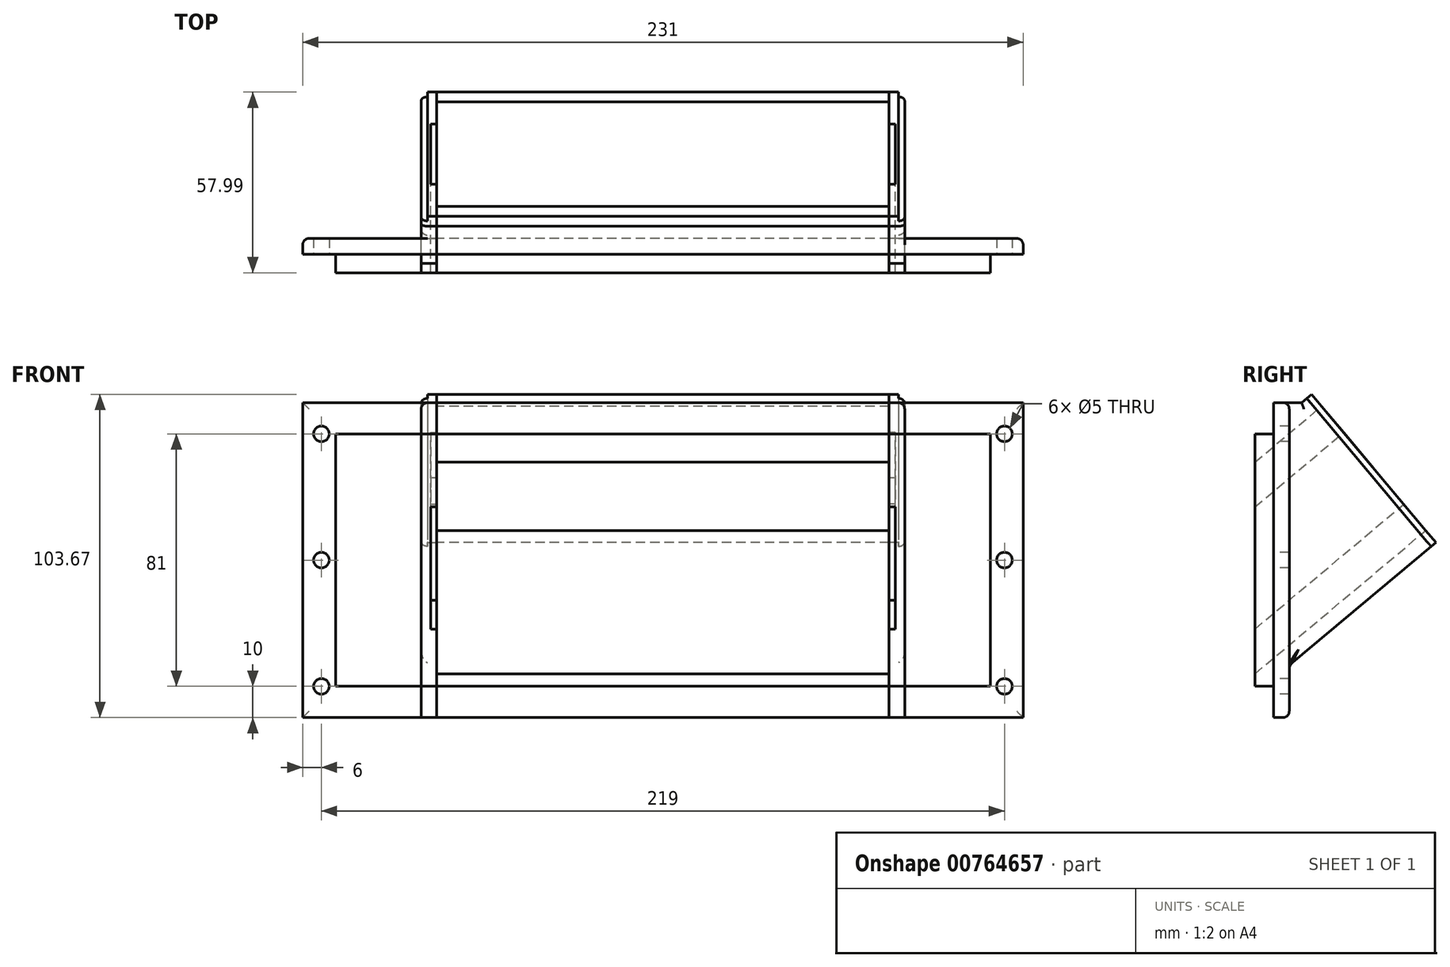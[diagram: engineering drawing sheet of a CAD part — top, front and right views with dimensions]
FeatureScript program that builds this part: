
annotation { "Feature Type Name" : "Feature", "Feature Type Description" : "" }
export const myFeature = defineFeature(function(context is Context, id is Id, definition is map)
    precondition{}
    {
        {
            var Q0;
            Q0=qCreatedBy(makeId("Right.planeOp"),FACE);
            var sketch = newSketch(context, id + "F0", { "sketchPlane" : qUnion([Q0])});
            skLineSegment(sketch, "E0", {"start": v(-6, 71.92) * mm, "end": v(-6, 81) * mm});
            skLineSegment(sketch, "E1", {"start": v(-6, 0) * mm, "end": v(-6, 4.04) * mm});
            skLineSegment(sketch, "E2", {"start": v(-6, 81) * mm, "end": v(0, 81) * mm});
            skLineSegment(sketch, "E3", {"start": v(-6, 0) * mm, "end": v(0, 0) * mm});
            skLineSegment(sketch, "E4", {"start": v(-3, 0.03) * mm, "end": v(-3, 0) * mm});
            skLineSegment(sketch, "E5", {"start": v(-3, 81) * mm, "end": v(-3, 80.97) * mm});
            skLineSegment(sketch, "E6", {"start": v(-6, 71.92) * mm, "end": v(15.35, 89.84) * mm});
            skLineSegment(sketch, "E7", {"start": v(-6, 4.04) * mm, "end": v(48.78, 50) * mm});
            skLineSegment(sketch, "E8", {"start": v(52, 46.18) * mm, "end": v(48.78, 50) * mm});
            skLineSegment(sketch, "E9", {"start": v(15.35, 89.84) * mm, "end": v(12.14, 93.67) * mm});
            skLineSegment(sketch, "E10", {"start": v(8.96, 91) * mm, "end": v(12.14, 93.67) * mm});
            skLineSegment(sketch, "E11", {"start": v(-3, 80.97) * mm, "end": v(-2.96, 81) * mm});
            skLineSegment(sketch, "E12", {"start": v(5, 6.75) * mm, "end": v(52, 46.18) * mm});
            skLineSegment(sketch, "E13", {"start": v(-3.04, 0) * mm, "end": v(-3, 0.03) * mm});
            skLineSegment(sketch, "E14", {"start": v(0, -10) * mm, "end": v(0, 0) * mm});
            skLineSegment(sketch, "E15", {"start": v(0, 81) * mm, "end": v(0, 91) * mm});
            skLineSegment(sketch, "E16", {"start": v(0, -10) * mm, "end": v(5, -10) * mm});
            skLineSegment(sketch, "E17", {"start": v(5, -10) * mm, "end": v(5, -5) * mm});
            skLineSegment(sketch, "E18", {"start": v(5, -5) * mm, "end": v(5, 0) * mm});
            skLineSegment(sketch, "E19", {"start": v(5, 0) * mm, "end": v(5, 5) * mm});
            skLineSegment(sketch, "E20", {"start": v(5, 5) * mm, "end": v(5, 6.75) * mm});
            skLineSegment(sketch, "E21", {"start": v(0, 91) * mm, "end": v(5, 91) * mm});
            skLineSegment(sketch, "E22", {"start": v(5, 91) * mm, "end": v(8.96, 91) * mm});
            skSolve(sketch);
        }
        {
            var Q0;
            Q0 = qSketchRegion(id + "F0", true);
            extrude(context, id + "F1", {"entities" : qUnion([Q0]), "depth" : 145 * mm, "offsetDistance" : 25 * mm});
        }
        {
            var Q0;
            Q0=qCreatedBy(makeId("Right.planeOp"),FACE);
            var sketch = newSketch(context, id + "F2", { "sketchPlane" : qUnion([Q0])});
            skLineSegment(sketch, "E23", {"start": v(-6, 71.92) * mm, "end": v(-6, 81) * mm});
            skLineSegment(sketch, "E24", {"start": v(-6, 0) * mm, "end": v(-6, 4.04) * mm});
            skLineSegment(sketch, "E25", {"start": v(-6, 81) * mm, "end": v(0, 81) * mm});
            skLineSegment(sketch, "E26", {"start": v(-6, 0) * mm, "end": v(0, 0) * mm});
            skLineSegment(sketch, "E27", {"start": v(-3, 0.03) * mm, "end": v(-3, 0) * mm});
            skLineSegment(sketch, "E28", {"start": v(-3, 81) * mm, "end": v(-3, 80.97) * mm});
            skLineSegment(sketch, "E29", {"start": v(52, 46.18) * mm, "end": v(48.78, 50) * mm});
            skLineSegment(sketch, "E30", {"start": v(15.35, 89.84) * mm, "end": v(12.14, 93.67) * mm});
            skLineSegment(sketch, "E31", {"start": v(8.96, 91) * mm, "end": v(12.14, 93.67) * mm});
            skLineSegment(sketch, "E32", {"start": v(-3, 80.97) * mm, "end": v(-2.96, 81) * mm});
            skLineSegment(sketch, "E33", {"start": v(5, 6.75) * mm, "end": v(52, 46.18) * mm});
            skLineSegment(sketch, "E34", {"start": v(-3.04, 0) * mm, "end": v(-3, 0.03) * mm});
            skLineSegment(sketch, "E35", {"start": v(0, -10) * mm, "end": v(0, 0) * mm});
            skLineSegment(sketch, "E36", {"start": v(0, 81) * mm, "end": v(0, 91) * mm});
            skLineSegment(sketch, "E37", {"start": v(0, -10) * mm, "end": v(5, -10) * mm});
            skLineSegment(sketch, "E38", {"start": v(5, -10) * mm, "end": v(5, -5) * mm});
            skLineSegment(sketch, "E39", {"start": v(5, -5) * mm, "end": v(5, 0) * mm});
            skLineSegment(sketch, "E40", {"start": v(5, 0) * mm, "end": v(5, 5) * mm});
            skLineSegment(sketch, "E41", {"start": v(5, 5) * mm, "end": v(5, 6.75) * mm});
            skLineSegment(sketch, "E42", {"start": v(0, 91) * mm, "end": v(5, 91) * mm});
            skLineSegment(sketch, "E43", {"start": v(5, 91) * mm, "end": v(8.96, 91) * mm});
            skLineSegment(sketch, "E44", {"start": v(15.35, 89.84) * mm, "end": v(48.78, 50) * mm});
            skLineSegment(sketch, "E45", {"start": v(-6, 71.92) * mm, "end": v(-6, 4.04) * mm});
            skSolve(sketch);
        }
        {
            var Q0;
            {var subQ5=sQuery(id+"F2.wireOp",EDGE,"E23");Q0=makeQuery(id+"F2.imprint","IMPRINT",FACE,{"disambiguationData":[TD([[makeQuery(id+"F2.imprint","IMPRINT",EDGE,{"derivedFrom":subQ5}),-1.0]])]});}
            extrude(context, id + "F3", {"entities" : qUnion([Q0]), "depth" : -5 * mm, "offsetDistance" : 25 * mm});
        }
        {
            var Q0;
            Q0=qCreatedBy(makeId("Right.planeOp"),FACE);
            var sketch = newSketch(context, id + "F4", { "sketchPlane" : qUnion([Q0])});
            skLineSegment(sketch, "E46", {"start": v(-6, 71.92) * mm, "end": v(-6, 81) * mm});
            skLineSegment(sketch, "E47", {"start": v(-6, 0) * mm, "end": v(-6, 4.04) * mm});
            skLineSegment(sketch, "E48", {"start": v(-6, 81) * mm, "end": v(0, 81) * mm});
            skLineSegment(sketch, "E49", {"start": v(-6, 0) * mm, "end": v(0, 0) * mm});
            skLineSegment(sketch, "E50", {"start": v(-3, 0.03) * mm, "end": v(-3, 0) * mm});
            skLineSegment(sketch, "E51", {"start": v(-3, 81) * mm, "end": v(-3, 80.97) * mm});
            skLineSegment(sketch, "E52", {"start": v(52, 46.18) * mm, "end": v(48.78, 50) * mm});
            skLineSegment(sketch, "E53", {"start": v(15.35, 89.84) * mm, "end": v(12.14, 93.67) * mm});
            skLineSegment(sketch, "E54", {"start": v(8.96, 91) * mm, "end": v(12.14, 93.67) * mm});
            skLineSegment(sketch, "E55", {"start": v(-3, 80.97) * mm, "end": v(-2.96, 81) * mm});
            skLineSegment(sketch, "E56", {"start": v(5, 6.75) * mm, "end": v(52, 46.18) * mm});
            skLineSegment(sketch, "E57", {"start": v(-3.04, 0) * mm, "end": v(-3, 0.03) * mm});
            skLineSegment(sketch, "E58", {"start": v(0, -10) * mm, "end": v(0, 0) * mm});
            skLineSegment(sketch, "E59", {"start": v(0, 81) * mm, "end": v(0, 91) * mm});
            skLineSegment(sketch, "E60", {"start": v(0, -10) * mm, "end": v(5, -10) * mm});
            skLineSegment(sketch, "E61", {"start": v(5, -10) * mm, "end": v(5, -5) * mm});
            skLineSegment(sketch, "E62", {"start": v(5, -5) * mm, "end": v(5, 0) * mm});
            skLineSegment(sketch, "E63", {"start": v(5, 0) * mm, "end": v(5, 5) * mm});
            skLineSegment(sketch, "E64", {"start": v(5, 5) * mm, "end": v(5, 6.75) * mm});
            skLineSegment(sketch, "E65", {"start": v(0, 91) * mm, "end": v(5, 91) * mm});
            skLineSegment(sketch, "E66", {"start": v(5, 91) * mm, "end": v(8.96, 91) * mm});
            skLineSegment(sketch, "E67", {"start": v(15.35, 89.84) * mm, "end": v(48.78, 50) * mm});
            skLineSegment(sketch, "E68", {"start": v(-6, 71.92) * mm, "end": v(-6, 4.04) * mm});
            skSolve(sketch);
        }
        {
            var Q0;
            Q0=qCreatedBy(makeId("Right.planeOp"),FACE);
            cPlane(context, id + "F5", {"entities" : qUnion([Q0]), "cplaneType" : CPlaneType.OFFSET, "offset" : 145 * mm, "width" : 150 * mm, "height" : 150 * mm});
        }
        {
            var Q0;
            Q0=qCreatedBy(id+"F5.planeOp",FACE);
            var sketch = newSketch(context, id + "F6", { "sketchPlane" : qUnion([Q0])});
            skLineSegment(sketch, "E69", {"start": v(-6, 71.92) * mm, "end": v(-6, 81) * mm});
            skLineSegment(sketch, "E70", {"start": v(-6, 0) * mm, "end": v(-6, 4.04) * mm});
            skLineSegment(sketch, "E71", {"start": v(-6, 81) * mm, "end": v(0, 81) * mm});
            skLineSegment(sketch, "E72", {"start": v(-6, 0) * mm, "end": v(0, 0) * mm});
            skLineSegment(sketch, "E73", {"start": v(-3, 0.03) * mm, "end": v(-3, 0) * mm});
            skLineSegment(sketch, "E74", {"start": v(-3, 81) * mm, "end": v(-3, 80.97) * mm});
            skLineSegment(sketch, "E75", {"start": v(52, 46.18) * mm, "end": v(48.78, 50) * mm});
            skLineSegment(sketch, "E76", {"start": v(15.35, 89.84) * mm, "end": v(12.14, 93.67) * mm});
            skLineSegment(sketch, "E77", {"start": v(8.96, 91) * mm, "end": v(12.14, 93.67) * mm});
            skLineSegment(sketch, "E78", {"start": v(-3, 80.97) * mm, "end": v(-2.96, 81) * mm});
            skLineSegment(sketch, "E79", {"start": v(5, 6.75) * mm, "end": v(52, 46.18) * mm});
            skLineSegment(sketch, "E80", {"start": v(-3.04, 0) * mm, "end": v(-3, 0.03) * mm});
            skLineSegment(sketch, "E81", {"start": v(0, -10) * mm, "end": v(0, 0) * mm});
            skLineSegment(sketch, "E82", {"start": v(0, 81) * mm, "end": v(0, 91) * mm});
            skLineSegment(sketch, "E83", {"start": v(0, -10) * mm, "end": v(5, -10) * mm});
            skLineSegment(sketch, "E84", {"start": v(5, -10) * mm, "end": v(5, -5) * mm});
            skLineSegment(sketch, "E85", {"start": v(5, -5) * mm, "end": v(5, 0) * mm});
            skLineSegment(sketch, "E86", {"start": v(5, 0) * mm, "end": v(5, 5) * mm});
            skLineSegment(sketch, "E87", {"start": v(5, 5) * mm, "end": v(5, 6.75) * mm});
            skLineSegment(sketch, "E88", {"start": v(0, 91) * mm, "end": v(5, 91) * mm});
            skLineSegment(sketch, "E89", {"start": v(5, 91) * mm, "end": v(8.96, 91) * mm});
            skLineSegment(sketch, "E90", {"start": v(15.35, 89.84) * mm, "end": v(48.78, 50) * mm});
            skLineSegment(sketch, "E91", {"start": v(-6, 71.92) * mm, "end": v(-6, 4.04) * mm});
            skSolve(sketch);
        }
        {
            var Q0;
            {var subQ5=sQuery(id+"F6.wireOp",EDGE,"E69");Q0=makeQuery(id+"F6.imprint","IMPRINT",FACE,{"disambiguationData":[TD([[makeQuery(id+"F6.imprint","IMPRINT",EDGE,{"derivedFrom":subQ5}),-1.0]])]});}
            extrude(context, id + "F7", {"entities" : qUnion([Q0]), "depth" : 5 * mm, "offsetDistance" : 25 * mm});
        }
        {
            var Q0;
            Q0=qCreatedBy(id+"F5.planeOp",FACE);
            var sketch = newSketch(context, id + "F8", { "sketchPlane" : qUnion([Q0])});
            skLineSegment(sketch, "E92", {"start": v(-6, 71.92) * mm, "end": v(-6, 81) * mm});
            skLineSegment(sketch, "E93", {"start": v(-6, 0) * mm, "end": v(-6, 4.04) * mm});
            skLineSegment(sketch, "E94", {"start": v(-6, 81) * mm, "end": v(0, 81) * mm});
            skLineSegment(sketch, "E95", {"start": v(-6, 0) * mm, "end": v(0, 0) * mm});
            skLineSegment(sketch, "E96", {"start": v(-3, 0.03) * mm, "end": v(-3, 0) * mm});
            skLineSegment(sketch, "E97", {"start": v(-3, 81) * mm, "end": v(-3, 80.97) * mm});
            skLineSegment(sketch, "E98", {"start": v(-3, 80.97) * mm, "end": v(-2.96, 81) * mm});
            skLineSegment(sketch, "E99", {"start": v(-3.04, 0) * mm, "end": v(-3, 0.03) * mm});
            skLineSegment(sketch, "E100", {"start": v(0, -10) * mm, "end": v(0, 0) * mm});
            skLineSegment(sketch, "E101", {"start": v(0, 81) * mm, "end": v(0, 91) * mm});
            skLineSegment(sketch, "E102", {"start": v(0, -10) * mm, "end": v(5, -10) * mm});
            skLineSegment(sketch, "E103", {"start": v(5, -10) * mm, "end": v(5, -5) * mm});
            skLineSegment(sketch, "E104", {"start": v(5, -5) * mm, "end": v(5, 0) * mm});
            skLineSegment(sketch, "E105", {"start": v(5, 0) * mm, "end": v(5, 5) * mm});
            skLineSegment(sketch, "E106", {"start": v(5, 5) * mm, "end": v(5, 6.75) * mm});
            skLineSegment(sketch, "E107", {"start": v(0, 91) * mm, "end": v(5, 91) * mm});
            skLineSegment(sketch, "E108", {"start": v(-6, 71.92) * mm, "end": v(-6, 4.04) * mm});
            skLineSegment(sketch, "E109", {"start": v(5, 6.75) * mm, "end": v(5, 91) * mm});
            skSolve(sketch);
        }
        {
            var Q0;
            Q0 = qSketchRegion(id + "F8", true);
            extrude(context, id + "F9", {"entities" : qUnion([Q0]), "depth" : 43 * mm, "offsetDistance" : 25 * mm});
        }
        {
            var Q0;
            Q0=qCreatedBy(makeId("Right.planeOp"),FACE);
            var sketch = newSketch(context, id + "F10", { "sketchPlane" : qUnion([Q0])});
            skLineSegment(sketch, "E110", {"start": v(-6, 71.92) * mm, "end": v(-6, 81) * mm});
            skLineSegment(sketch, "E111", {"start": v(-6, 0) * mm, "end": v(-6, 4.04) * mm});
            skLineSegment(sketch, "E112", {"start": v(-6, 81) * mm, "end": v(0, 81) * mm});
            skLineSegment(sketch, "E113", {"start": v(-6, 0) * mm, "end": v(0, 0) * mm});
            skLineSegment(sketch, "E114", {"start": v(-3, 0.03) * mm, "end": v(-3, 0) * mm});
            skLineSegment(sketch, "E115", {"start": v(-3, 81) * mm, "end": v(-3, 80.97) * mm});
            skLineSegment(sketch, "E116", {"start": v(-3, 80.97) * mm, "end": v(-2.96, 81) * mm});
            skLineSegment(sketch, "E117", {"start": v(-3.04, 0) * mm, "end": v(-3, 0.03) * mm});
            skLineSegment(sketch, "E118", {"start": v(0, -10) * mm, "end": v(0, 0) * mm});
            skLineSegment(sketch, "E119", {"start": v(0, 81) * mm, "end": v(0, 91) * mm});
            skLineSegment(sketch, "E120", {"start": v(0, -10) * mm, "end": v(5, -10) * mm});
            skLineSegment(sketch, "E121", {"start": v(5, -10) * mm, "end": v(5, -5) * mm});
            skLineSegment(sketch, "E122", {"start": v(5, -5) * mm, "end": v(5, 0) * mm});
            skLineSegment(sketch, "E123", {"start": v(5, 0) * mm, "end": v(5, 5) * mm});
            skLineSegment(sketch, "E124", {"start": v(5, 5) * mm, "end": v(5, 6.75) * mm});
            skLineSegment(sketch, "E125", {"start": v(0, 91) * mm, "end": v(5, 91) * mm});
            skLineSegment(sketch, "E126", {"start": v(-6, 71.92) * mm, "end": v(-6, 4.04) * mm});
            skLineSegment(sketch, "E127", {"start": v(5, 6.75) * mm, "end": v(5, 91) * mm});
            skSolve(sketch);
        }
        {
            var Q0;
            Q0 = qSketchRegion(id + "F10", true);
            extrude(context, id + "F11", {"entities" : qUnion([Q0]), "depth" : -43 * mm, "offsetDistance" : 25 * mm});
        }
        {
            var Q0;
            Q0=qCreatedBy(makeId("Front.planeOp"),FACE);
            var sketch = newSketch(context, id + "F12", { "sketchPlane" : qUnion([Q0])});
            skLineSegment(sketch, "E128.bottom", {"start": v(-43, 0) * mm, "end": v(-32.5, 0) * mm});
            skLineSegment(sketch, "E128.top", {"start": v(-43, 81) * mm, "end": v(-32.5, 81) * mm});
            skLineSegment(sketch, "E128.left", {"start": v(-43, 0) * mm, "end": v(-43, 81) * mm});
            skLineSegment(sketch, "E128.right", {"start": v(-32.5, 0) * mm, "end": v(-32.5, 81) * mm});
            skLineSegment(sketch, "E129.bottom", {"start": v(188, 0) * mm, "end": v(177.5, 0) * mm});
            skLineSegment(sketch, "E129.top", {"start": v(188, 81) * mm, "end": v(177.5, 81) * mm});
            skLineSegment(sketch, "E129.left", {"start": v(188, 0) * mm, "end": v(188, 81) * mm});
            skLineSegment(sketch, "E129.right", {"start": v(177.5, 0) * mm, "end": v(177.5, 81) * mm});
            skSolve(sketch);
        }
        {
            var Q0;
            Q0 = qSketchRegion(id + "F12", true);
            extrude(context, id + "F13", {"entities" : qUnion([Q0]), "operationType" : NewBodyOperationType.REMOVE, "oppositeDirection" : true, "depth" : -7 * mm, "offsetDistance" : 25 * mm});
        }
        {
            var Q0;
            Q0=qCreatedBy(id+"F5.planeOp",FACE);
            cPlane(context, id + "F14", {"entities" : qUnion([Q0]), "cplaneType" : CPlaneType.OFFSET, "offset" : 5 * mm, "width" : 150 * mm, "height" : 150 * mm});
        }
        {
            var Q0;
            Q0=qCreatedBy(makeId("Right.planeOp"),FACE);
            cPlane(context, id + "F15", {"entities" : qUnion([Q0]), "cplaneType" : CPlaneType.OFFSET, "offset" : 5 * mm, "oppositeDirection" : true, "width" : 150 * mm, "height" : 150 * mm});
        }
        {
            var Q0;
            Q0=qCreatedBy(id+"F14.planeOp",FACE);
            var sketch = newSketch(context, id + "F16", { "sketchPlane" : qUnion([Q0])});
            skLineSegment(sketch, "E130", {"start": v(12.14, 93.67) * mm, "end": v(52, 46.18) * mm});
            skLineSegment(sketch, "E131", {"start": v(10.6, 92.39) * mm, "end": v(50.46, 44.9) * mm});
            skLineSegment(sketch, "E132", {"start": v(10.6, 92.39) * mm, "end": v(12.14, 93.67) * mm});
            skLineSegment(sketch, "E133", {"start": v(50.46, 44.9) * mm, "end": v(52, 46.18) * mm});
            skSolve(sketch);
        }
        {
            var Q0;
            Q0 = qSketchRegion(id + "F16", true);
            extrude(context, id + "F17", {"entities" : qUnion([Q0]), "operationType" : NewBodyOperationType.REMOVE, "oppositeDirection" : true, "depth" : 2 * mm, "offsetDistance" : 25 * mm});
        }
        {
            var Q0;
            Q0=qCreatedBy(id+"F15.planeOp",FACE);
            var sketch = newSketch(context, id + "F18", { "sketchPlane" : qUnion([Q0])});
            skLineSegment(sketch, "E134", {"start": v(12.14, 93.67) * mm, "end": v(52, 46.18) * mm});
            skLineSegment(sketch, "E135", {"start": v(10.6, 92.39) * mm, "end": v(50.46, 44.9) * mm});
            skLineSegment(sketch, "E136", {"start": v(10.6, 92.39) * mm, "end": v(12.14, 93.67) * mm});
            skLineSegment(sketch, "E137", {"start": v(50.46, 44.9) * mm, "end": v(52, 46.18) * mm});
            skSolve(sketch);
        }
        {
            var Q0;
            Q0=makeQuery(id+"F18.imprint","IMPRINT",FACE,{"disambiguationData":[TD([[makeQuery(id+"F18.imprint","IMPRINT",EDGE,{"derivedFrom":sQuery(id+"F18.wireOp",EDGE,"E134")}),-1.0]])]});
            extrude(context, id + "F19", {"entities" : qUnion([Q0]), "operationType" : NewBodyOperationType.REMOVE, "oppositeDirection" : true, "depth" : -2 * mm, "offsetDistance" : 25 * mm});
        }
        {
            var Q0;
            Q0=qCreatedBy(makeId("Front.planeOp"),FACE);
            var sketch = newSketch(context, id + "F20", { "sketchPlane" : qUnion([Q0])});
            skPoint(sketch, "E138", {"position": v(-37, 81) * mm});
            skPoint(sketch, "E139", {"position": v(-37, 40.5) * mm});
            skPoint(sketch, "E140", {"position": v(-37, 0) * mm});
            skPoint(sketch, "E141", {"position": v(182, 0) * mm});
            skPoint(sketch, "E142", {"position": v(182, 40.5) * mm});
            skPoint(sketch, "E143", {"position": v(182, 81) * mm});
            skSolve(sketch);
        }
        {
            var Q0;
            Q0=sQuery(id+"F20.wireOp",VERTEX,"E138");
            var Q1;
            Q1=sQuery(id+"F20.wireOp",VERTEX,"E139");
            var Q2;
            Q2=sQuery(id+"F20.wireOp",VERTEX,"E140");
            var Q3;
            Q3=sQuery(id+"F20.wireOp",VERTEX,"E143");
            var Q4;
            Q4=sQuery(id+"F20.wireOp",VERTEX,"E142");
            var Q5;
            Q5=sQuery(id+"F20.wireOp",VERTEX,"E141");
            var Q6;
            Q6=makeQuery(id+"F9.opExtrude","SWEPT_BODY",BODY,{"disambiguationData":[OSD([sQuery(id+"F8.wireOp",EDGE,"E92"),sQuery(id+"F8.wireOp",EDGE,"E93"),sQuery(id+"F8.wireOp",EDGE,"E94"),sQuery(id+"F8.wireOp",EDGE,"E95"),sQuery(id+"F8.wireOp",EDGE,"E100"),sQuery(id+"F8.wireOp",EDGE,"E101"),sQuery(id+"F8.wireOp",EDGE,"E102"),sQuery(id+"F8.wireOp",EDGE,"E103"),sQuery(id+"F8.wireOp",EDGE,"E104"),sQuery(id+"F8.wireOp",EDGE,"E105"),sQuery(id+"F8.wireOp",EDGE,"E106"),sQuery(id+"F8.wireOp",EDGE,"E107"),sQuery(id+"F8.wireOp",EDGE,"E108"),sQuery(id+"F8.wireOp",EDGE,"E109")])]});
            var Q7;
            Q7=makeQuery(id+"F11.opExtrude","SWEPT_BODY",BODY,{"disambiguationData":[OSD([sQuery(id+"F10.wireOp",EDGE,"E110"),sQuery(id+"F10.wireOp",EDGE,"E111"),sQuery(id+"F10.wireOp",EDGE,"E112"),sQuery(id+"F10.wireOp",EDGE,"E113"),sQuery(id+"F10.wireOp",EDGE,"E118"),sQuery(id+"F10.wireOp",EDGE,"E119"),sQuery(id+"F10.wireOp",EDGE,"E120"),sQuery(id+"F10.wireOp",EDGE,"E121"),sQuery(id+"F10.wireOp",EDGE,"E122"),sQuery(id+"F10.wireOp",EDGE,"E123"),sQuery(id+"F10.wireOp",EDGE,"E124"),sQuery(id+"F10.wireOp",EDGE,"E125"),sQuery(id+"F10.wireOp",EDGE,"E126"),sQuery(id+"F10.wireOp",EDGE,"E127")])]});
            hole(context, id + "F21", {"style" : HoleStyle.SIMPLE, "endStyle" : HoleEndStyle.THROUGH, "holeDiameter" : 5 * mm, "majorDiameter" : 5 * mm, "isTappedThrough" : true, "tappedDepth" : 12 * mm, "tapClearance" : 3, "locations" : qUnion([Q0, Q1, Q2, Q3, Q4, Q5]), "scope" : qUnion([Q6, Q7])});
        }
        {
            var Q0;
            Q0=makeQuery(id+"F9.opExtrude","SWEPT_EDGE",EDGE,{"disambiguationData":[OSD([sQuery(id+"F8.wireOp",EDGE,"E107"),sQuery(id+"F8.wireOp",EDGE,"E109")])]});
            var Q1;
            Q1=makeQuery(id+"F9.opExtrude","CAP_EDGE",EDGE,{"disambiguationData":[OSD([sQuery(id+"F8.wireOp",EDGE,"E103"),sQuery(id+"F8.wireOp",EDGE,"E104"),sQuery(id+"F8.wireOp",EDGE,"E105"),sQuery(id+"F8.wireOp",EDGE,"E106"),sQuery(id+"F8.wireOp",EDGE,"E109")])],"isStart":false});
            var Q2;
            Q2=makeQuery(id+"F9.opExtrude","SWEPT_EDGE",EDGE,{"disambiguationData":[OSD([sQuery(id+"F8.wireOp",EDGE,"E102"),sQuery(id+"F8.wireOp",EDGE,"E103")])]});
            var Q3;
            Q3=makeQuery(id+"F7.opExtrude","SWEPT_EDGE",EDGE,{"disambiguationData":[OSD([sQuery(id+"F6.wireOp",EDGE,"E83"),sQuery(id+"F6.wireOp",EDGE,"E84")])]});
            var Q4;
            Q4=makeQuery(id+"F3.opExtrude","SWEPT_EDGE",EDGE,{"disambiguationData":[OSD([sQuery(id+"F2.wireOp",EDGE,"E37"),sQuery(id+"F2.wireOp",EDGE,"E38")])]});
            var Q5;
            Q5=makeQuery(id+"F11.opExtrude","SWEPT_EDGE",EDGE,{"disambiguationData":[OSD([sQuery(id+"F10.wireOp",EDGE,"E120"),sQuery(id+"F10.wireOp",EDGE,"E121")])]});
            var Q6;
            Q6=makeQuery(id+"F1.opExtrude","SWEPT_EDGE",EDGE,{"disambiguationData":[OSD([sQuery(id+"F0.wireOp",EDGE,"E16"),sQuery(id+"F0.wireOp",EDGE,"E17")])]});
            var Q7;
            Q7=makeQuery(id+"F11.opExtrude","CAP_EDGE",EDGE,{"disambiguationData":[OSD([sQuery(id+"F10.wireOp",EDGE,"E121"),sQuery(id+"F10.wireOp",EDGE,"E122"),sQuery(id+"F10.wireOp",EDGE,"E123"),sQuery(id+"F10.wireOp",EDGE,"E124"),sQuery(id+"F10.wireOp",EDGE,"E127")])],"isStart":false});
            var Q8;
            Q8=makeQuery(id+"F11.opExtrude","SWEPT_EDGE",EDGE,{"disambiguationData":[OSD([sQuery(id+"F10.wireOp",EDGE,"E125"),sQuery(id+"F10.wireOp",EDGE,"E127")])]});
            var Q9;
            Q9=makeQuery(id+"F3.opExtrude","CAP_EDGE",EDGE,{"disambiguationData":[OSD([sQuery(id+"F2.wireOp",EDGE,"E42"),sQuery(id+"F2.wireOp",EDGE,"E43")])],"isStart":false});
            var Q10;
            Q10=makeQuery(id+"F3.opExtrude","CAP_EDGE",EDGE,{"disambiguationData":[OSD([sQuery(id+"F2.wireOp",EDGE,"E33")])],"isStart":false});
            var Q11;
            Q11=makeQuery(id+"F7.opExtrude","CAP_EDGE",EDGE,{"disambiguationData":[OSD([sQuery(id+"F6.wireOp",EDGE,"E79")])],"isStart":false});
            var Q12;
            Q12=makeQuery(id+"F7.opExtrude","CAP_EDGE",EDGE,{"disambiguationData":[OSD([sQuery(id+"F6.wireOp",EDGE,"E88"),sQuery(id+"F6.wireOp",EDGE,"E89")])],"isStart":false});
            var Q13;
            Q13=makeQuery(id+"F7.opExtrude","CAP_EDGE",EDGE,{"disambiguationData":[OSD([sQuery(id+"F6.wireOp",EDGE,"E77")])],"isStart":false});
            var Q14;
            Q14=makeQuery(id+"F3.opExtrude","CAP_EDGE",EDGE,{"disambiguationData":[OSD([sQuery(id+"F2.wireOp",EDGE,"E31")])],"isStart":false});
            fillet(context, id + "F22", {"entities" : qUnion([Q0, Q1, Q2, Q3, Q4, Q5, Q6, Q7, Q8, Q9, Q10, Q11, Q12, Q13, Q14]), "radius" : 2 * mm, "tangentPropagation" : true, "allowEdgeOverflow" : false});
        }
        {
            var Q0;
            Q0=qCreatedBy(makeId("Right.planeOp"),FACE);
            var sketch = newSketch(context, id + "F23", { "sketchPlane" : qUnion([Q0])});
            skLineSegment(sketch, "E144", {"start": v(22.42, 81.41) * mm, "end": v(41.7, 58.43) * mm});
            skLineSegment(sketch, "E145", {"start": v(-6, 57.56) * mm, "end": v(-6, 18.4) * mm});
            skLineSegment(sketch, "E146", {"start": v(-6, 57.56) * mm, "end": v(22.42, 81.41) * mm});
            skLineSegment(sketch, "E147", {"start": v(-6, 18.4) * mm, "end": v(41.7, 58.43) * mm});
            skSolve(sketch);
        }
        {
            var Q0;
            Q0=qCreatedBy(id+"F5.planeOp",FACE);
            var sketch = newSketch(context, id + "F24", { "sketchPlane" : qUnion([Q0])});
            skLineSegment(sketch, "E148", {"start": v(22.42, 81.41) * mm, "end": v(41.7, 58.43) * mm});
            skLineSegment(sketch, "E149", {"start": v(-6, 57.56) * mm, "end": v(-6, 18.4) * mm});
            skLineSegment(sketch, "E150", {"start": v(-6, 57.56) * mm, "end": v(22.42, 81.41) * mm});
            skLineSegment(sketch, "E151", {"start": v(-6, 18.4) * mm, "end": v(41.7, 58.43) * mm});
            skSolve(sketch);
        }
        {
            var Q0;
            Q0 = qSketchRegion(id + "F23", true);
            extrude(context, id + "F25", {"entities" : qUnion([Q0]), "operationType" : NewBodyOperationType.REMOVE, "oppositeDirection" : true, "depth" : 2 * mm, "offsetDistance" : 25 * mm});
        }
        {
            var Q0;
            Q0 = qSketchRegion(id + "F24", true);
            extrude(context, id + "F26", {"entities" : qUnion([Q0]), "operationType" : NewBodyOperationType.REMOVE, "depth" : 2 * mm, "offsetDistance" : 25 * mm});
        }
        {
            var Q0;
            Q0=makeQuery(id+"F1.opExtrude","SWEPT_EDGE",EDGE,{"disambiguationData":[OSD([sQuery(id+"F0.wireOp",EDGE,"E12"),sQuery(id+"F0.wireOp",EDGE,"E20")])]});
            var Q1;
            Q1=makeQuery(id+"F7.opExtrude","SWEPT_EDGE",EDGE,{"disambiguationData":[OSD([sQuery(id+"F6.wireOp",EDGE,"E79"),sQuery(id+"F6.wireOp",EDGE,"E87")])]});
            var Q2;
            Q2=makeQuery(id+"F3.opExtrude","SWEPT_EDGE",EDGE,{"disambiguationData":[OSD([sQuery(id+"F2.wireOp",EDGE,"E33"),sQuery(id+"F2.wireOp",EDGE,"E41")])]});
            fillet(context, id + "F27", {"entities" : qUnion([Q0, Q1, Q2]), "radius" : 3 * mm, "tangentPropagation" : true, "allowEdgeOverflow" : false});
        }
    });
